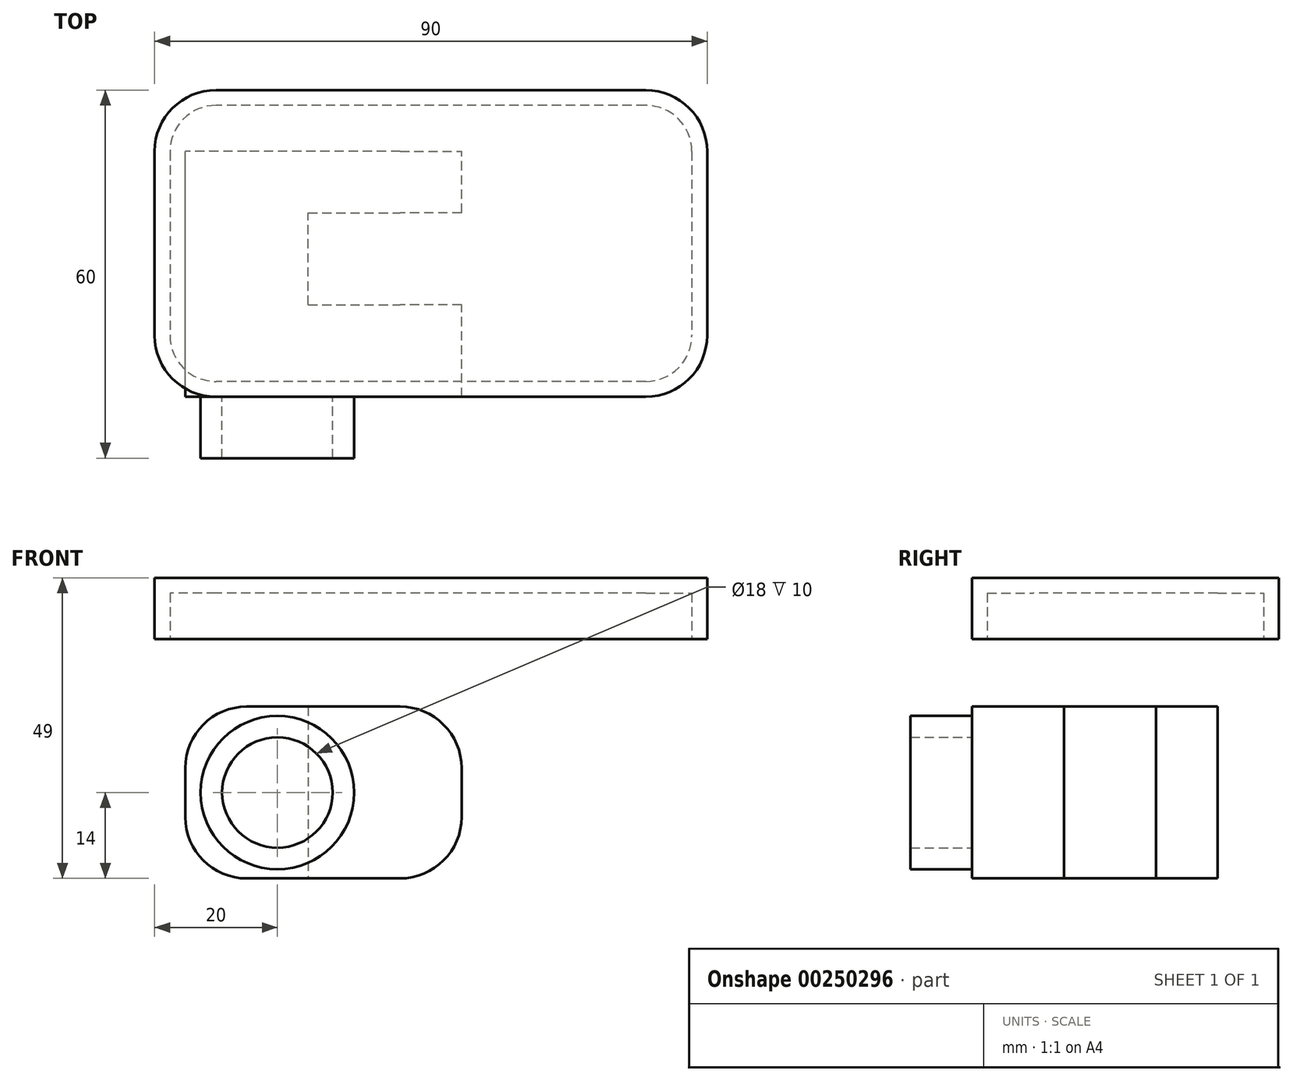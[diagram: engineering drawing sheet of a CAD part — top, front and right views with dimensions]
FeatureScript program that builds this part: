
annotation { "Feature Type Name" : "Feature", "Feature Type Description" : "" }
export const myFeature = defineFeature(function(context is Context, id is Id, definition is map)
    precondition{}
    {
        {
            var Q0;
            Q0=qCreatedBy(makeId("Front.planeOp"),FACE);
            var sketch = newSketch(context, id + "F0", { "sketchPlane" : qUnion([Q0])});
            skLineSegment(sketch, "E0.bottom", {"start": v(35, 25) * mm, "end": v(-35, 25) * mm});
            skLineSegment(sketch, "E0.top", {"start": v(35, -25) * mm, "end": v(-35, -25) * mm});
            skLineSegment(sketch, "E0.left", {"start": v(45, 15) * mm, "end": v(45, -15) * mm});
            skLineSegment(sketch, "E0.right", {"start": v(-45, 15) * mm, "end": v(-45, -15) * mm});
            skPoint(sketch, "E0.middle", {"position": v(0, 0) * mm});
            skPoint(sketch, "E1.visualSharp", {"position": v(45, 25) * mm});
            skArc(sketch, "E1.filletArc", {"start": v(45, 15) * mm, "mid": v(42.07, 22.07) * mm, "end": v(35, 25) * mm});
            skPoint(sketch, "E2.visualSharp", {"position": v(45, -25) * mm});
            skArc(sketch, "E2.filletArc", {"start": v(35, -25) * mm, "mid": v(42.07, -22.07) * mm, "end": v(45, -15) * mm});
            skPoint(sketch, "E3.visualSharp", {"position": v(-45, -25) * mm});
            skArc(sketch, "E3.filletArc", {"start": v(-45, -15) * mm, "mid": v(-42.07, -22.07) * mm, "end": v(-35, -25) * mm});
            skPoint(sketch, "E4.visualSharp", {"position": v(-45, 25) * mm});
            skArc(sketch, "E4.filletArc", {"start": v(-35, 25) * mm, "mid": v(-42.07, 22.07) * mm, "end": v(-45, 15) * mm});
            skSolve(sketch);
        }
        {
            var Q0;
            Q0 = qSketchRegion(id + "F0", true);
            extrude(context, id + "F1", {"entities" : qUnion([Q0]), "depth" : 10 * mm});
        }
        {
            var Q0;
            Q0=makeQuery(id+"F1.opExtrude","CAP_FACE",FACE,{"disambiguationData":[OSD([sQuery(id+"F0.wireOp",EDGE,"E0.bottom"),sQuery(id+"F0.wireOp",EDGE,"E0.top"),sQuery(id+"F0.wireOp",EDGE,"E0.left"),sQuery(id+"F0.wireOp",EDGE,"E0.right"),sQuery(id+"F0.wireOp",EDGE,"E1.filletArc"),sQuery(id+"F0.wireOp",EDGE,"E2.filletArc"),sQuery(id+"F0.wireOp",EDGE,"E3.filletArc"),sQuery(id+"F0.wireOp",EDGE,"E4.filletArc")])],"isStart":false});
            var sketch = newSketch(context, id + "F2", { "sketchPlane" : qUnion([Q0])});
            skLineSegment(sketch, "E5.bottom", {"start": v(-5, 14) * mm, "end": v(-30, 14) * mm});
            skLineSegment(sketch, "E5.top", {"start": v(-5, -14) * mm, "end": v(-30, -14) * mm});
            skLineSegment(sketch, "E5.left", {"start": v(5, 4) * mm, "end": v(5, -4) * mm});
            skLineSegment(sketch, "E5.right", {"start": v(-40, 4) * mm, "end": v(-40, -4) * mm});
            skPoint(sketch, "E5.middle", {"position": v(-17.5, 0) * mm});
            skPoint(sketch, "E6.visualSharp", {"position": v(-40, -14) * mm});
            skArc(sketch, "E6.filletArc", {"start": v(-40, -4) * mm, "mid": v(-37.07, -11.07) * mm, "end": v(-30, -14) * mm});
            skPoint(sketch, "E7.visualSharp", {"position": v(5, -14) * mm});
            skArc(sketch, "E7.filletArc", {"start": v(-5, -14) * mm, "mid": v(2.07, -11.07) * mm, "end": v(5, -4) * mm});
            skPoint(sketch, "E8.visualSharp", {"position": v(5, 14) * mm});
            skArc(sketch, "E8.filletArc", {"start": v(5, 4) * mm, "mid": v(2.07, 11.07) * mm, "end": v(-5, 14) * mm});
            skPoint(sketch, "E9.visualSharp", {"position": v(-40, 14) * mm});
            skArc(sketch, "E9.filletArc", {"start": v(-30, 14) * mm, "mid": v(-37.07, 11.07) * mm, "end": v(-40, 4) * mm});
            skSolve(sketch);
        }
        {
            var Q0;
            Q0 = qSketchRegion(id + "F2", true);
            extrude(context, id + "F3", {"entities" : qUnion([Q0]), "depth" : 40 * mm});
        }
        {
            var Q0;
            Q0=makeQuery(id+"F3.opExtrude","CAP_FACE",FACE,{"disambiguationData":[OSD([sQuery(id+"F2.wireOp",EDGE,"E5.bottom"),sQuery(id+"F2.wireOp",EDGE,"E5.top"),sQuery(id+"F2.wireOp",EDGE,"E5.left"),sQuery(id+"F2.wireOp",EDGE,"E5.right"),sQuery(id+"F2.wireOp",EDGE,"E6.filletArc"),sQuery(id+"F2.wireOp",EDGE,"E7.filletArc"),sQuery(id+"F2.wireOp",EDGE,"E8.filletArc"),sQuery(id+"F2.wireOp",EDGE,"E9.filletArc")])],"isStart":false});
            var sketch = newSketch(context, id + "F4", { "sketchPlane" : qUnion([Q0])});
            skLineSegment(sketch, "E10", {"start": v(-12.7, 0) * mm, "end": v(-36.08, 0) * mm, "construction": true});
            skLineSegment(sketch, "E11", {"start": v(-25, 8.89) * mm, "end": v(-25, -10.98) * mm, "construction": true});
            skCircle(sketch, "E12", {"center": v(-25, 0) * mm, "radius": 9 * mm});
            skCircle(sketch, "E13", {"center": v(-25, 0) * mm, "radius": 12.5 * mm});
            skSolve(sketch);
        }
        {
            var Q0;
            Q0 = qSketchRegion(id + "F4", true);
            extrude(context, id + "F5", {"entities" : qUnion([Q0]), "depth" : 10 * mm});
        }
        {
            var Q0;
            Q0=qCreatedBy(makeId("Top.planeOp"),FACE);
            var sketch = newSketch(context, id + "F6", { "sketchPlane" : qUnion([Q0])});
            skLineSegment(sketch, "E14.bottom", {"start": v(-20, -35) * mm, "end": v(30, -35) * mm});
            skLineSegment(sketch, "E14.top", {"start": v(-20, -20) * mm, "end": v(30, -20) * mm});
            skLineSegment(sketch, "E14.left", {"start": v(-20, -35) * mm, "end": v(-20, -20) * mm});
            skLineSegment(sketch, "E14.right", {"start": v(30, -35) * mm, "end": v(30, -20) * mm});
            skPoint(sketch, "E14.middle", {"position": v(5, -27.5) * mm});
            skSolve(sketch);
        }
        {
            var Q0;
            Q0=makeQuery(id+"F6.imprint","IMPRINT",FACE,{"disambiguationData":[TD([[makeQuery(id+"F6.imprint","IMPRINT",EDGE,{"derivedFrom":sQuery(id+"F6.wireOp",EDGE,"E14.bottom")}),1.0]])]});
            extrude(context, id + "F7", {"entities" : qUnion([Q0]), "endBound" : BoundingType.SYMMETRIC, "depth" : 68 * mm});
        }
        {
            var Q0;
            Q0=makeQuery(id+"F7.opExtrude","SWEPT_BODY",BODY,{"disambiguationData":[OSD([sQuery(id+"F6.wireOp",EDGE,"E14.bottom"),sQuery(id+"F6.wireOp",EDGE,"E14.top"),sQuery(id+"F6.wireOp",EDGE,"E14.left"),sQuery(id+"F6.wireOp",EDGE,"E14.right")])]});
            var Q1;
            Q1=makeQuery(id+"F3.opExtrude","SWEPT_BODY",BODY,{"disambiguationData":[OSD([sQuery(id+"F2.wireOp",EDGE,"E5.bottom"),sQuery(id+"F2.wireOp",EDGE,"E5.top"),sQuery(id+"F2.wireOp",EDGE,"E5.left"),sQuery(id+"F2.wireOp",EDGE,"E5.right"),sQuery(id+"F2.wireOp",EDGE,"E6.filletArc"),sQuery(id+"F2.wireOp",EDGE,"E7.filletArc"),sQuery(id+"F2.wireOp",EDGE,"E8.filletArc"),sQuery(id+"F2.wireOp",EDGE,"E9.filletArc")])]});
            booleanBodies(context, id + "F8", {"operationType" : BooleanOperationType.SUBTRACTION, "tools" : qUnion([Q0]), "targets" : qUnion([Q1])});
        }
        {
            var Q0;
            Q0=makeQuery(id+"F1.opExtrude","SWEPT_BODY",BODY,{"disambiguationData":[OSD([sQuery(id+"F0.wireOp",EDGE,"E0.bottom"),sQuery(id+"F0.wireOp",EDGE,"E0.top"),sQuery(id+"F0.wireOp",EDGE,"E0.left"),sQuery(id+"F0.wireOp",EDGE,"E0.right"),sQuery(id+"F0.wireOp",EDGE,"E1.filletArc"),sQuery(id+"F0.wireOp",EDGE,"E2.filletArc"),sQuery(id+"F0.wireOp",EDGE,"E3.filletArc"),sQuery(id+"F0.wireOp",EDGE,"E4.filletArc")])]});
            var Q1;
            Q1=makeQuery(id+"F1.opExtrude","CAP_EDGE",EDGE,{"disambiguationData":[OSD([sQuery(id+"F0.wireOp",EDGE,"E0.bottom")])],"isStart":true});
            transform(context, id + "F9", {"entities" : qUnion([Q0]), "transformType" : TransformType.ROTATION, "transformAxis" : qUnion([Q1]), "angle" : 90 * degree, "makeCopy" : false});
        }
        {
            var Q0;
            Q0=makeQuery(id+"F1.opExtrude","CAP_FACE",FACE,{"disambiguationData":[OSD([sQuery(id+"F0.wireOp",EDGE,"E0.bottom"),sQuery(id+"F0.wireOp",EDGE,"E0.top"),sQuery(id+"F0.wireOp",EDGE,"E0.left"),sQuery(id+"F0.wireOp",EDGE,"E0.right"),sQuery(id+"F0.wireOp",EDGE,"E1.filletArc"),sQuery(id+"F0.wireOp",EDGE,"E2.filletArc"),sQuery(id+"F0.wireOp",EDGE,"E3.filletArc"),sQuery(id+"F0.wireOp",EDGE,"E4.filletArc")])],"isStart":true});
            shell(context, id + "F10", {"entities" : qUnion([Q0]), "thickness" : 2.5 * mm});
        }
    });
